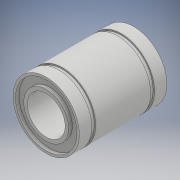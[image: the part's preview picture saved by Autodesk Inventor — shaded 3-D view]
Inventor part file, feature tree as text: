
AUTODESK INVENTOR PART (.ipt)
format: ipt  version: 2018 (Build 220112000, 112)  size: 168,448 bytes
history: native  units: mm
features: other x3, sketch x1
ambient origin geometry x8: Origin, YZ Plane, XZ Plane, XY Plane, X Axis, Y Axis, Z Axis, Center Point
bodies: Body1 (feature_tree)
feature tree (4):
  other  "Sólido1"
  other  "Revolução1"
  other  "Revolução2"
  sketch  "Esboço3"  dims[d0=13.0mm d1=37.0mm d4=0.55mm d5=1.6mm d6=1.6mm d8=1.0mm d23=90.0deg d24=90.0deg d26=26.5mm d27=5.25mm d28=37.0mm d30=8.0mm d31=34.0mm d32=37.0mm d33=1.5mm d34=5.0mm d36=1.5mm d37=1.5mm]
